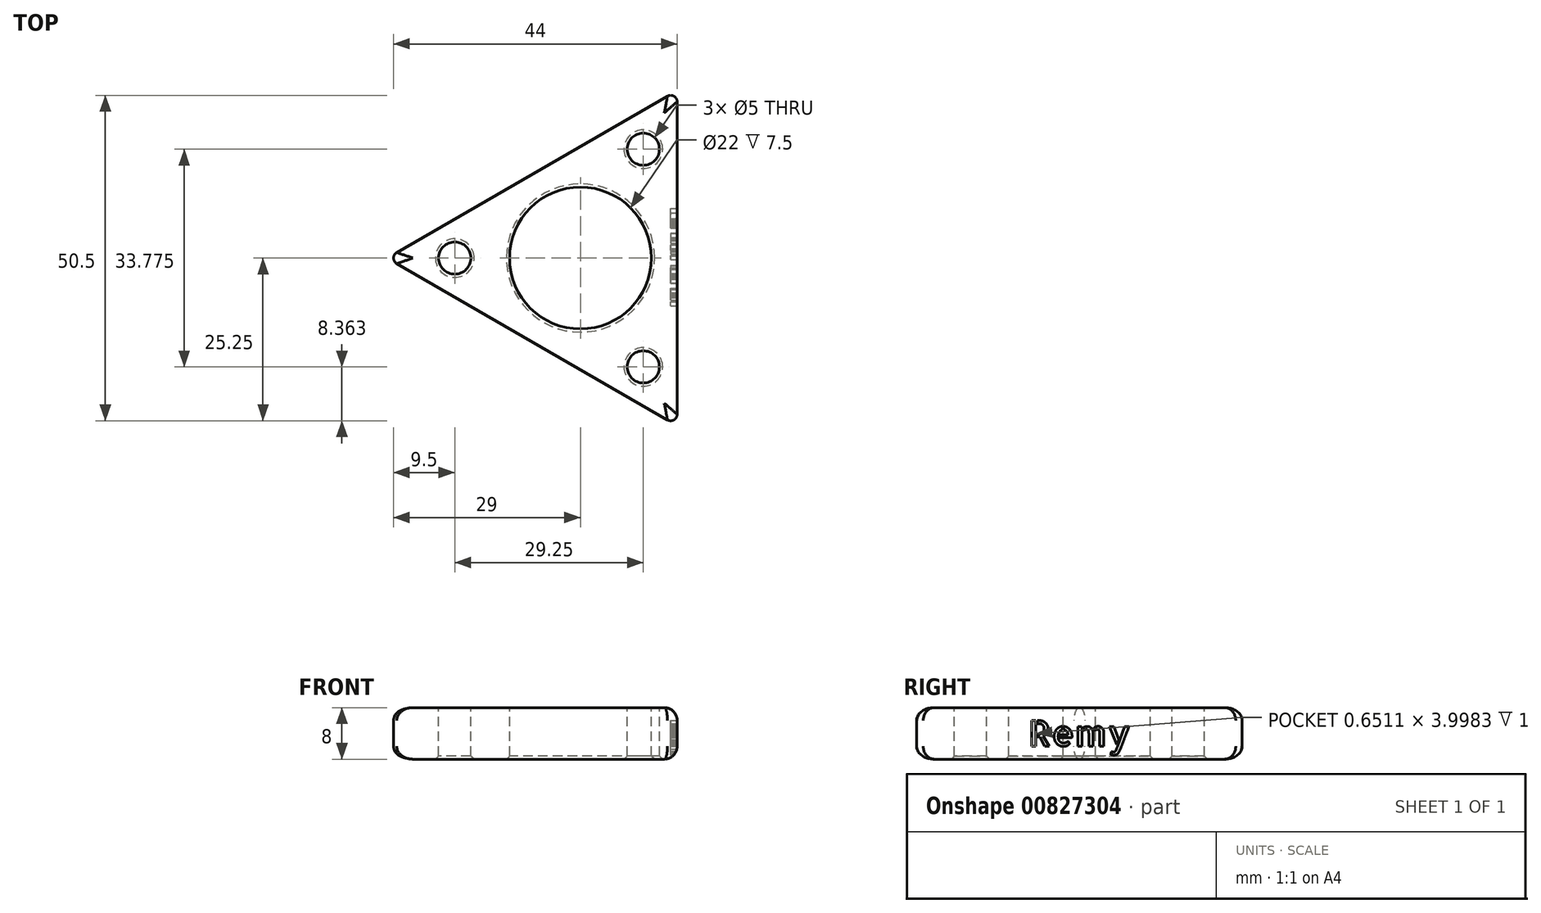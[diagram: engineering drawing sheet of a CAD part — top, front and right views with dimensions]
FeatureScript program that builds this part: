
annotation { "Feature Type Name" : "Feature", "Feature Type Description" : "" }
export const myFeature = defineFeature(function(context is Context, id is Id, definition is map)
    precondition{}
    {
        {
            var Q0;
            Q0=qCreatedBy(makeId("Top.planeOp"),FACE);
            var sketch = newSketch(context, id + "F0", { "sketchPlane" : qUnion([Q0])});
            skCircle(sketch, "E0.cCircle", {"center": v(0, 0) * mm, "radius": 15 * mm, "construction": true});
            skLineSegment(sketch, "E0.0", {"start": v(15, 25.98) * mm, "end": v(15, -25.98) * mm});
            skLineSegment(sketch, "E0.1", {"start": v(15, -25.98) * mm, "end": v(-30, 0) * mm});
            skLineSegment(sketch, "E0.2", {"start": v(-30, 0) * mm, "end": v(15, 25.98) * mm});
            skPoint(sketch, "E0.0.midPoint", {"position": v(15, 0) * mm});
            skSolve(sketch);
        }
        {
            var Q0;
            Q0=makeQuery(id+"F0.imprint","IMPRINT",FACE,{"disambiguationData":[TD([[makeQuery(id+"F0.imprint","IMPRINT",EDGE,{"derivedFrom":sQuery(id+"F0.wireOp",EDGE,"E0.0")}),-1.0]])]});
            extrude(context, id + "F1", {"entities" : qUnion([Q0]), "depth" : 8 * mm, "offsetDistance" : 25 * mm});
        }
        {
            var Q0;
            Q0=makeQuery(id+"F1.opExtrude","CAP_FACE",FACE,{"disambiguationData":[OSD([sQuery(id+"F0.wireOp",EDGE,"E0.0"),sQuery(id+"F0.wireOp",EDGE,"E0.1"),sQuery(id+"F0.wireOp",EDGE,"E0.2")])],"isStart":false});
            var sketch = newSketch(context, id + "F2", { "sketchPlane" : qUnion([Q0])});
            skCircle(sketch, "E1", {"center": v(0, 0) * mm, "radius": 11 * mm});
            skCircle(sketch, "E2", {"center": v(-19.5, 0) * mm, "radius": 2.5 * mm});
            skCircle(sketch, "E3", {"center": v(9.75, 16.89) * mm, "radius": 2.5 * mm});
            skCircle(sketch, "E4", {"center": v(9.75, -16.89) * mm, "radius": 2.5 * mm});
            skSolve(sketch);
        }
        {
            var Q0;
            Q0=makeQuery(id+"F2.imprint","IMPRINT",FACE,{"disambiguationData":[TD([[makeQuery(id+"F2.imprint","IMPRINT",EDGE,{"derivedFrom":sQuery(id+"F2.wireOp",EDGE,"E1")}),1.0]])]});
            var Q1;
            Q1=makeQuery(id+"F2.imprint","IMPRINT",FACE,{"disambiguationData":[TD([[makeQuery(id+"F2.imprint","IMPRINT",EDGE,{"derivedFrom":sQuery(id+"F2.wireOp",EDGE,"E2")}),1.0]])]});
            var Q2;
            Q2=makeQuery(id+"F2.imprint","IMPRINT",FACE,{"disambiguationData":[TD([[makeQuery(id+"F2.imprint","IMPRINT",EDGE,{"derivedFrom":sQuery(id+"F2.wireOp",EDGE,"E3")}),1.0]])]});
            var Q3;
            Q3=makeQuery(id+"F2.imprint","IMPRINT",FACE,{"disambiguationData":[TD([[makeQuery(id+"F2.imprint","IMPRINT",EDGE,{"derivedFrom":sQuery(id+"F2.wireOp",EDGE,"E4")}),1.0]])]});
            extrude(context, id + "F3", {"entities" : qUnion([Q0, Q1, Q2, Q3]), "operationType" : NewBodyOperationType.REMOVE, "endBound" : BoundingType.THROUGH_ALL, "oppositeDirection" : true, "depth" : 25 * mm, "offsetDistance" : 25 * mm});
        }
        {
            var Q0;
            Q0=makeQuery(id+"F3.boolean.opBoolean","COPY",EDGE,{"derivedFrom":makeQuery(id+"F3.opExtrude","CAP_EDGE",EDGE,{"disambiguationData":[OSD([sQuery(id+"F2.wireOp",EDGE,"E1")])],"isStart":true})});
            var Q1;
            Q1=makeQuery(id+"F3.boolean.opBoolean","INTERSECT",EDGE,{"derivedFrom":[makeQuery(id+"F1.opExtrude","CAP_FACE",FACE,{"disambiguationData":[OSD([sQuery(id+"F0.wireOp",EDGE,"E0.0"),sQuery(id+"F0.wireOp",EDGE,"E0.1"),sQuery(id+"F0.wireOp",EDGE,"E0.2")])],"isStart":true}),makeQuery(id+"F3.opExtrude","SWEPT_FACE",FACE,{"disambiguationData":[OSD([sQuery(id+"F2.wireOp",EDGE,"E1")])]})]});
            var Q2;
            Q2=makeQuery(id+"F3.boolean.opBoolean","COPY",EDGE,{"derivedFrom":makeQuery(id+"F3.opExtrude","CAP_EDGE",EDGE,{"disambiguationData":[OSD([sQuery(id+"F2.wireOp",EDGE,"E2")])],"isStart":true})});
            var Q3;
            Q3=makeQuery(id+"F3.boolean.opBoolean","COPY",EDGE,{"derivedFrom":makeQuery(id+"F3.opExtrude","CAP_EDGE",EDGE,{"disambiguationData":[OSD([sQuery(id+"F2.wireOp",EDGE,"E3")])],"isStart":true})});
            var Q4;
            Q4=makeQuery(id+"F3.boolean.opBoolean","COPY",EDGE,{"derivedFrom":makeQuery(id+"F3.opExtrude","CAP_EDGE",EDGE,{"disambiguationData":[OSD([sQuery(id+"F2.wireOp",EDGE,"E4")])],"isStart":true})});
            var Q5;
            Q5=makeQuery(id+"F3.boolean.opBoolean","INTERSECT",EDGE,{"derivedFrom":[makeQuery(id+"F1.opExtrude","CAP_FACE",FACE,{"disambiguationData":[OSD([sQuery(id+"F0.wireOp",EDGE,"E0.0"),sQuery(id+"F0.wireOp",EDGE,"E0.1"),sQuery(id+"F0.wireOp",EDGE,"E0.2")])],"isStart":true}),makeQuery(id+"F3.opExtrude","SWEPT_FACE",FACE,{"disambiguationData":[OSD([sQuery(id+"F2.wireOp",EDGE,"E2")])]})]});
            var Q6;
            Q6=makeQuery(id+"F3.boolean.opBoolean","INTERSECT",EDGE,{"derivedFrom":[makeQuery(id+"F1.opExtrude","CAP_FACE",FACE,{"disambiguationData":[OSD([sQuery(id+"F0.wireOp",EDGE,"E0.0"),sQuery(id+"F0.wireOp",EDGE,"E0.1"),sQuery(id+"F0.wireOp",EDGE,"E0.2")])],"isStart":true}),makeQuery(id+"F3.opExtrude","SWEPT_FACE",FACE,{"disambiguationData":[OSD([sQuery(id+"F2.wireOp",EDGE,"E3")])]})]});
            var Q7;
            Q7=makeQuery(id+"F3.boolean.opBoolean","INTERSECT",EDGE,{"derivedFrom":[makeQuery(id+"F1.opExtrude","CAP_FACE",FACE,{"disambiguationData":[OSD([sQuery(id+"F0.wireOp",EDGE,"E0.0"),sQuery(id+"F0.wireOp",EDGE,"E0.1"),sQuery(id+"F0.wireOp",EDGE,"E0.2")])],"isStart":true}),makeQuery(id+"F3.opExtrude","SWEPT_FACE",FACE,{"disambiguationData":[OSD([sQuery(id+"F2.wireOp",EDGE,"E4")])]})]});
            chamfer(context, id + "F4", {"entities" : qUnion([Q0, Q1, Q2, Q3, Q4, Q5, Q6, Q7]), "width" : .5 * mm, "tangentPropagation" : true});
        }
        {
            var Q0;
            Q0=makeQuery(id+"F1.opExtrude","SWEPT_EDGE",EDGE,{"disambiguationData":[OSD([sQuery(id+"F0.wireOp",EDGE,"E0.1"),sQuery(id+"F0.wireOp",EDGE,"E0.2")])]});
            var Q1;
            Q1=makeQuery(id+"F1.opExtrude","SWEPT_EDGE",EDGE,{"disambiguationData":[OSD([sQuery(id+"F0.wireOp",EDGE,"E0.0"),sQuery(id+"F0.wireOp",EDGE,"E0.2")])]});
            var Q2;
            Q2=makeQuery(id+"F1.opExtrude","SWEPT_EDGE",EDGE,{"disambiguationData":[OSD([sQuery(id+"F0.wireOp",EDGE,"E0.0"),sQuery(id+"F0.wireOp",EDGE,"E0.1")])]});
            fillet(context, id + "F5", {"entities" : qUnion([Q0, Q1, Q2]), "radius" : 1 * mm, "tangentPropagation" : true, "allowEdgeOverflow" : false});
        }
        {
            var Q0;
            Q0=makeQuery(id+"F1.opExtrude","CAP_EDGE",EDGE,{"disambiguationData":[OSD([sQuery(id+"F0.wireOp",EDGE,"E0.2")])],"isStart":false});
            var Q1;
            Q1=makeQuery(id+"F1.opExtrude","CAP_EDGE",EDGE,{"disambiguationData":[OSD([sQuery(id+"F0.wireOp",EDGE,"E0.0")])],"isStart":false});
            var Q2;
            Q2=makeQuery(id+"F1.opExtrude","CAP_EDGE",EDGE,{"disambiguationData":[OSD([sQuery(id+"F0.wireOp",EDGE,"E0.1")])],"isStart":false});
            var Q3;
            Q3=makeQuery(id+"F1.opExtrude","CAP_EDGE",EDGE,{"disambiguationData":[OSD([sQuery(id+"F0.wireOp",EDGE,"E0.0")])],"isStart":true});
            var Q4;
            Q4=makeQuery(id+"F1.opExtrude","CAP_EDGE",EDGE,{"disambiguationData":[OSD([sQuery(id+"F0.wireOp",EDGE,"E0.1")])],"isStart":true});
            var Q5;
            Q5=makeQuery(id+"F1.opExtrude","CAP_EDGE",EDGE,{"disambiguationData":[OSD([sQuery(id+"F0.wireOp",EDGE,"E0.2")])],"isStart":true});
            fillet(context, id + "F6", {"entities" : qUnion([Q0, Q1, Q2, Q3, Q4, Q5]), "radius" : 2 * mm, "tangentPropagation" : true, "allowEdgeOverflow" : false});
        }
        {
            var Q0;
            Q0=makeQuery(id+"F1.opExtrude","SWEPT_FACE",FACE,{"disambiguationData":[OSD([sQuery(id+"F0.wireOp",EDGE,"E0.0")])]});
            var sketch = newSketch(context, id + "F7", { "sketchPlane" : qUnion([Q0])});
            skText(sketch, "E5", { "text": "Remy", "fontName": "AllertaStencil-Regular.ttf"});
            const initialGuessF7  = {"E5": [-0.0079, 0.002, 1, 0, 0.004]};
            skSetInitialGuess(sketch, initialGuessF7);
            skSolve(sketch);
        }
        {
            var Q0;
            Q0 = qSketchRegion(id + "F7", true);
            extrude(context, id + "F8", {"entities" : qUnion([Q0]), "operationType" : NewBodyOperationType.REMOVE, "oppositeDirection" : true, "depth" : 1 * mm, "offsetDistance" : 25 * mm});
        }
    });
